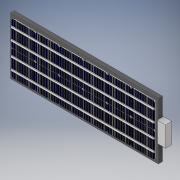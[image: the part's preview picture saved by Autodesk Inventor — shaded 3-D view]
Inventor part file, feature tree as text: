
AUTODESK INVENTOR PART (.ipt)
format: ipt  version: 2018 (Build 220112000, 112)  size: 712,192 bytes
history: native  units: in
note: dims shown in document units (in); Inventor stores cm internally (conversion verified against a paired STEP export)
features: sketch x7, extrude x6, pattern_linear x5
ambient origin geometry x8: Origin, YZ Plane, XZ Plane, XY Plane, X Axis, Y Axis, Z Axis, Center Point
bodies: Solid1 (feature_tree), Solid2 (feature_tree), Solid3 (feature_tree)
feature tree (18):
  extrude  "Extrusion1"  Depth=5.1181in
  extrude  "Extrusion2"  Depth=2.2835in
  pattern_linear  "Rectangular Pattern1"  Count1=6 Spacing1=2.3228in
  pattern_linear  "Rectangular Pattern2"  Count1=2 Spacing1=2.5in
  extrude  "Extrusion3"  Depth=4.9606in
  pattern_linear  "Rectangular Pattern3"  Spacing1=90.0deg  [1 undecoded]
  pattern_linear  "Rectangular Pattern4"  Spacing1=0.1772in  [1 undecoded]
  extrude  "Extrusion4"  Depth=4.9606in
  pattern_linear  "Rectangular Pattern5"  Spacing1=90.0deg  [1 undecoded]
  extrude  "Extrusion5"  Depth=0.0394in
  extrude  "Extrusion6"  Depth=0.0394in TaperAngle=0.0deg
  sketch  "Sketch7"  dims[d9=0.1181in d10=0.0in d11=2.3622in d13=2.3228in d14=0.7874in d16=2.5in d17=4.9606in d18=90.0deg d19=0.1772in d20=4.9606in d21=90.0deg d22=0.0394in d23=0.0394in d24=0.0in d25=5.1181in d27=0.1575in d28=2.3622in d30=2.3228in d31=13.8976in d32=0.1575in d33=0.5906in d34=0.7874in d36=1.122in d37=0.3937in d39=0.3937in d41=0.0787in d42=0.0in d43=0.7874in d45=2.4803in d46=0.1969in d47=0.3937in d48=0.0in d49=1.9685in d50=0.8019in d51=7.987in d52=0.9843in d53=0.5906in d54=0.0in]
  sketch  "Sketch1"  dims[d0=13.9764in d1=5.1181in]
  sketch  "Sketch2"  dims[d2=0.3937in d3=0.0in d4=2.2835in]
  sketch  "Sketch3"  dims[d5=2.4606in]
  sketch  "Sketch4"  dims[d6=0.0787in]
  sketch  "Sketch5"  dims[d7=0.0394in]
  sketch  "Sketch6"  dims[d8=0.1575in]
note: 3 required parameter values undecoded (feature->parameter linkage not recoverable at this tier; creation-order binding heuristic only, values carry confidence <= 0.55)
